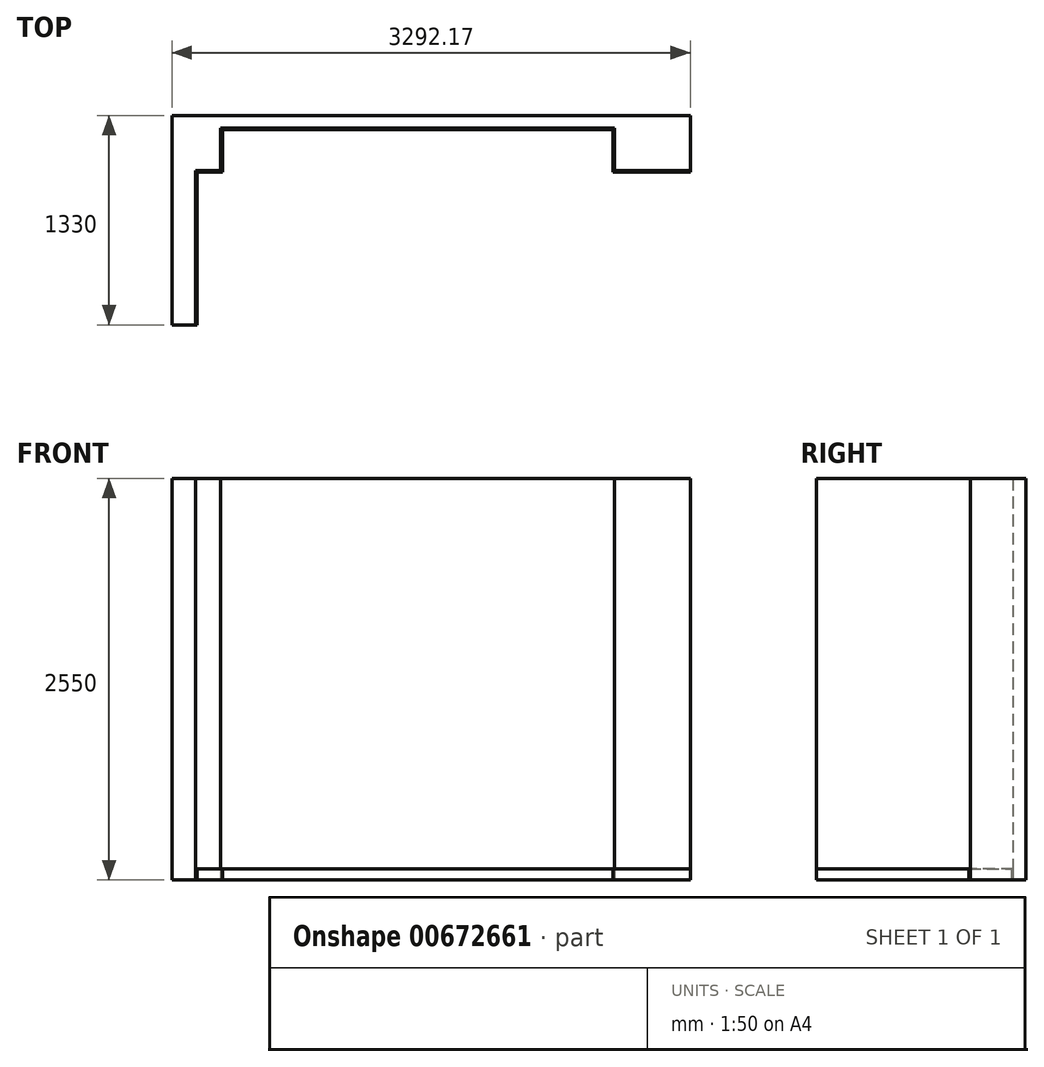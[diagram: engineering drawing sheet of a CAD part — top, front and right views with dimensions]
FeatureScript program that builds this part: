
annotation { "Feature Type Name" : "Feature", "Feature Type Description" : "" }
export const myFeature = defineFeature(function(context is Context, id is Id, definition is map)
    precondition{}
    {
        {
            var Q0;
            Q0=qCreatedBy(makeId("Top.planeOp"),FACE);
            var sketch = newSketch(context, id + "F0", { "sketchPlane" : qUnion([Q0])});
            skLineSegment(sketch, "E0", {"start": v(0, 0) * mm, "end": v(2500, 0) * mm});
            skLineSegment(sketch, "E1", {"start": v(2500, 0) * mm, "end": v(2500, -270) * mm});
            skLineSegment(sketch, "E2", {"start": v(2500, -270) * mm, "end": v(2982.17, -270) * mm});
            skLineSegment(sketch, "E3", {"start": v(2982.17, -270) * mm, "end": v(2982.17, 80) * mm});
            skLineSegment(sketch, "E4", {"start": v(2982.17, 80) * mm, "end": v(-310, 80) * mm});
            skLineSegment(sketch, "E5", {"start": v(-310, 80) * mm, "end": v(-310, -1250) * mm});
            skLineSegment(sketch, "E6", {"start": v(-310, -1250) * mm, "end": v(-160, -1250) * mm});
            skLineSegment(sketch, "E7", {"start": v(-160, -1250) * mm, "end": v(-160, -270) * mm});
            skLineSegment(sketch, "E8", {"start": v(-160, -270) * mm, "end": v(0, -270) * mm});
            skLineSegment(sketch, "E9", {"start": v(0, -270) * mm, "end": v(0, 0) * mm});
            skLineSegment(sketch, "E10", {"start": v(-150, -280) * mm, "end": v(10, -280) * mm});
            skLineSegment(sketch, "E11", {"start": v(10, -280) * mm, "end": v(10, -10) * mm});
            skLineSegment(sketch, "E12", {"start": v(10, -10) * mm, "end": v(2490, -10) * mm});
            skLineSegment(sketch, "E13", {"start": v(2490, -10) * mm, "end": v(2490, -280) * mm});
            skLineSegment(sketch, "E14", {"start": v(2490, -280) * mm, "end": v(2982.17, -280) * mm});
            skLineSegment(sketch, "E15", {"start": v(2982.17, -280) * mm, "end": v(2982.17, -270) * mm});
            skLineSegment(sketch, "E16", {"start": v(-150, -280) * mm, "end": v(-150, -1250) * mm});
            skLineSegment(sketch, "E17", {"start": v(-150, -1250) * mm, "end": v(-160, -1250) * mm});
            skSolve(sketch);
        }
        {
            var Q0;
            Q0=makeQuery(id+"F0.imprint","IMPRINT",FACE,{"disambiguationData":[TD([[makeQuery(id+"F0.imprint","IMPRINT",EDGE,{"derivedFrom":sQuery(id+"F0.wireOp",EDGE,"E0")}),1.0]])]});
            extrude(context, id + "F1", {"entities" : qUnion([Q0]), "depth" : 2550 * mm, "offsetDistance" : 25 * mm});
        }
        {
            var Q0;
            Q0=makeQuery(id+"F0.imprint","IMPRINT",FACE,{"disambiguationData":[TD([[makeQuery(id+"F0.imprint","IMPRINT",EDGE,{"derivedFrom":sQuery(id+"F0.wireOp",EDGE,"E0")}),-1.0]])]});
            extrude(context, id + "F2", {"entities" : qUnion([Q0]), "depth" : 70 * mm, "offsetDistance" : 25 * mm});
        }
    });
